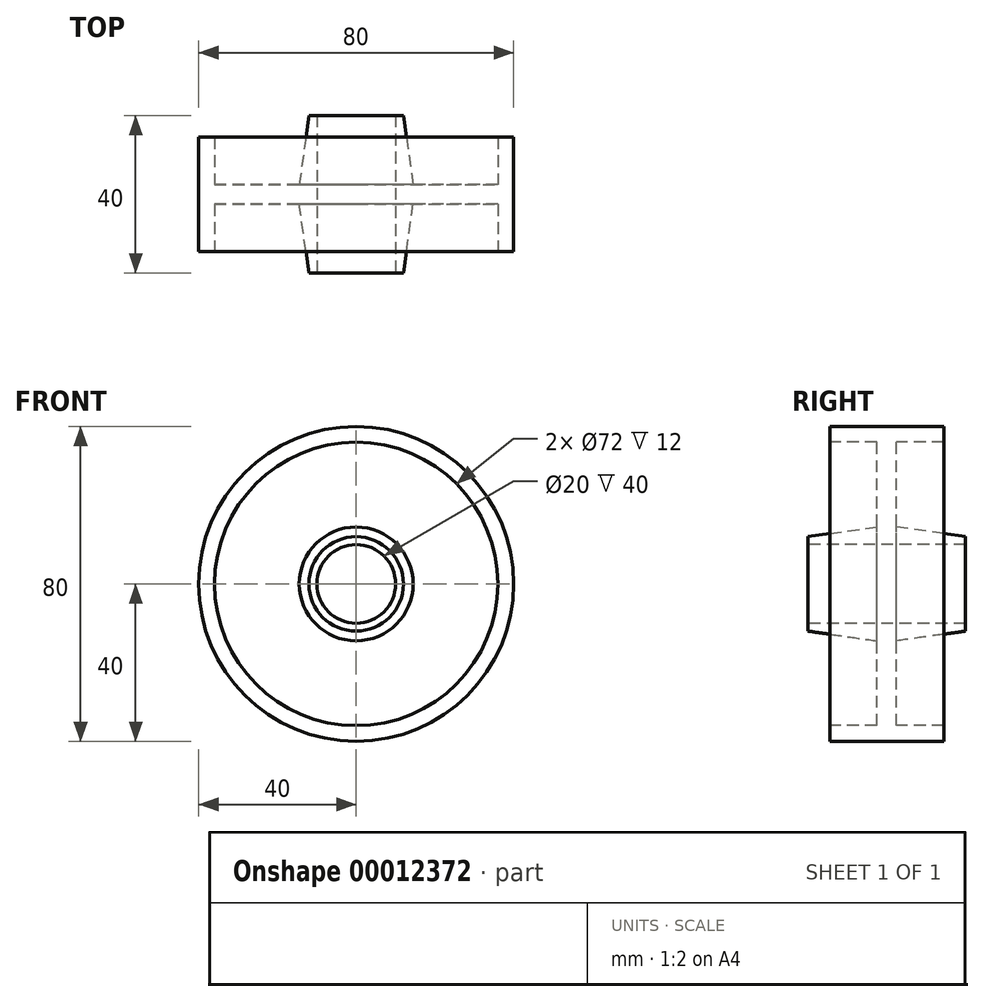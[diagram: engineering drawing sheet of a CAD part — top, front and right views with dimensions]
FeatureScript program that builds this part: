
annotation { "Feature Type Name" : "Feature", "Feature Type Description" : "" }
export const myFeature = defineFeature(function(context is Context, id is Id, definition is map)
    precondition{}
    {
        {
            var Q0;
            Q0=qCreatedBy(makeId("Top.planeOp"),FACE);
            var sketch = newSketch(context, id + "F0", { "sketchPlane" : qUnion([Q0])});
            skLineSegment(sketch, "E0.rect.bottom", {"start": v(-40, 14.5) * mm, "end": v(-36, 14.5) * mm});
            skLineSegment(sketch, "E0.rect.left", {"start": v(-40, 14.5) * mm, "end": v(-40, 0) * mm});
            skPoint(sketch, "E0.rect.middle", {"position": v(0, 0) * mm});
            skLineSegment(sketch, "E1.rect.left", {"start": v(-10, 20) * mm, "end": v(-10, 0) * mm});
            skLineSegment(sketch, "E2.rect.bottom", {"start": v(-12, 20) * mm, "end": v(-10, 20) * mm});
            skLineSegment(sketch, "E3", {"start": v(-12, 20) * mm, "end": v(-14.46, 2.5) * mm});
            skLineSegment(sketch, "E4.left", {"start": v(-40, 0) * mm, "end": v(-40, 14.5) * mm});
            skLineSegment(sketch, "E4.right", {"start": v(-36, 2.5) * mm, "end": v(-36, 14.5) * mm});
            skLineSegment(sketch, "E5.top", {"start": v(-14.46, 2.5) * mm, "end": v(-36, 2.5) * mm});
            skLineSegment(sketch, "E6.0.MirrorCS", {"start": v(-12, -20) * mm, "end": v(-10, -20) * mm});
            skLineSegment(sketch, "E6.1.MirrorCS", {"start": v(-40, -14.5) * mm, "end": v(-40, 0) * mm});
            skLineSegment(sketch, "E6.2.MirrorCS", {"start": v(-12, -20) * mm, "end": v(-14.46, -2.5) * mm});
            skLineSegment(sketch, "E6.3.MirrorCS", {"start": v(-36, -2.5) * mm, "end": v(-36, -14.5) * mm});
            skLineSegment(sketch, "E6.4.MirrorCS", {"start": v(-40, 0) * mm, "end": v(-40, -14.5) * mm});
            skLineSegment(sketch, "E6.5.MirrorCS", {"start": v(-40, -14.5) * mm, "end": v(-36, -14.5) * mm});
            skLineSegment(sketch, "E6.6.MirrorCS", {"start": v(-10, -20) * mm, "end": v(-10, 0) * mm});
            skLineSegment(sketch, "E6.7.MirrorCS", {"start": v(-14.46, -2.5) * mm, "end": v(-36, -2.5) * mm});
            skLineSegment(sketch, "E7", {"start": v(0, 0) * mm, "end": v(0, 26.14) * mm, "construction": true});
            skSolve(sketch);
        }
        {
            var Q0;
            Q0 = qSketchRegion(id + "F0", true);
            var Q1;
            Q1=sQuery(id+"F0.wireOp",EDGE,"E7");
            revolve(context, id + "F1", {"entities" : qUnion([Q0]), "axis" : qUnion([Q1]), "revolveType" : RevolveType.FULL});
        }
    });
